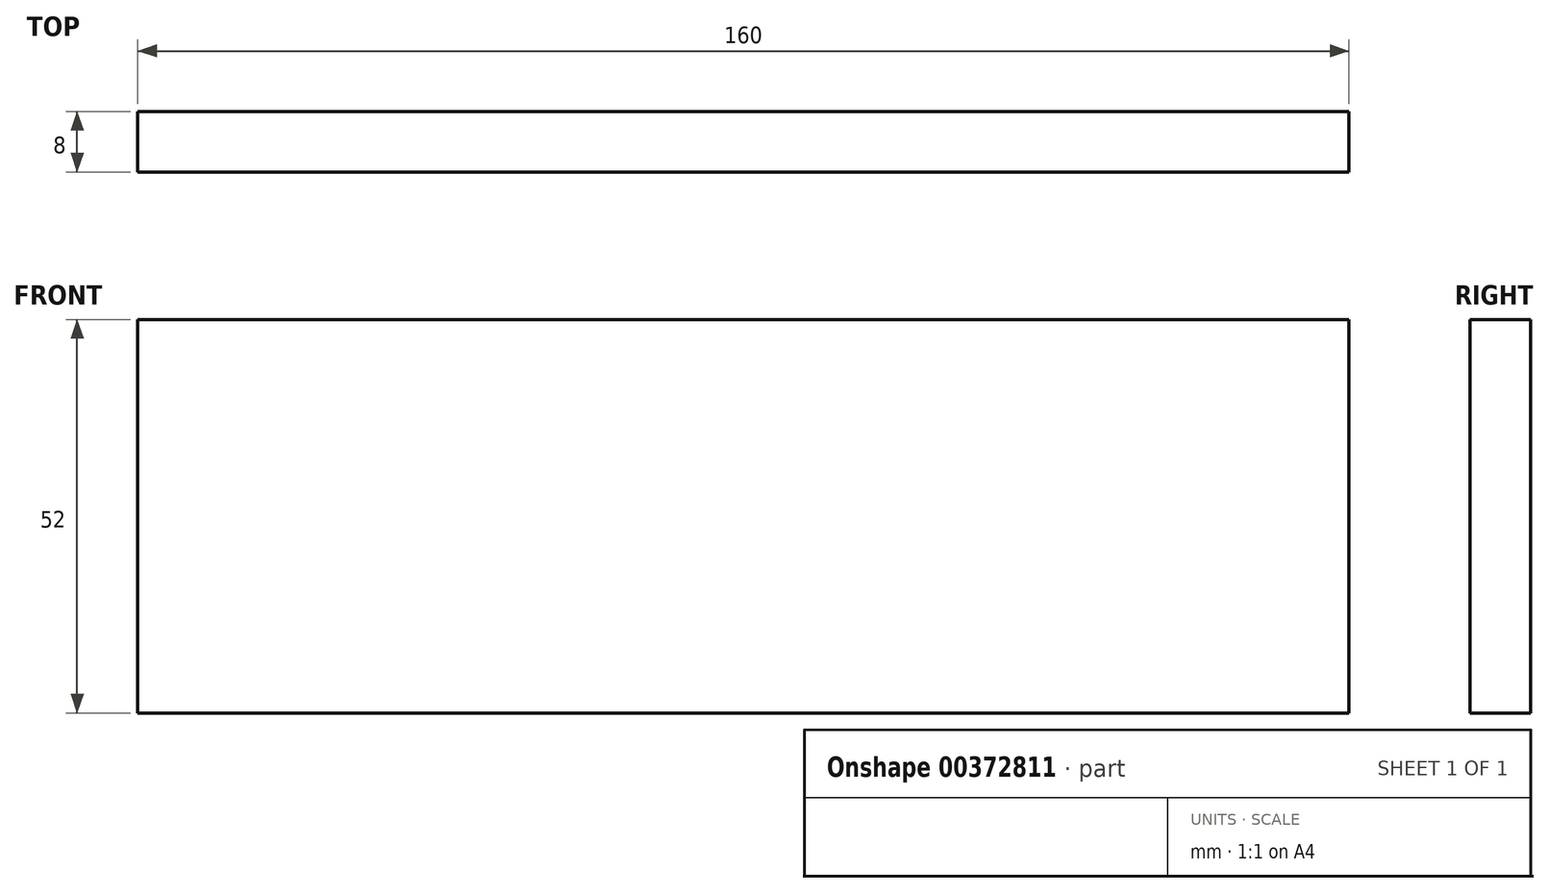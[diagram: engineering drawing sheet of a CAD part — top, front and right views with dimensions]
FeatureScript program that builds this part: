
annotation { "Feature Type Name" : "Feature", "Feature Type Description" : "" }
export const myFeature = defineFeature(function(context is Context, id is Id, definition is map)
    precondition{}
    {
        {
            var Q0;
            Q0=qCreatedBy(makeId("Front.planeOp"),FACE);
            var sketch = newSketch(context, id + "F0", { "sketchPlane" : qUnion([Q0])});
            skLineSegment(sketch, "E0.bottom", {"start": v(80, -26) * mm, "end": v(-80, -26) * mm});
            skLineSegment(sketch, "E0.top", {"start": v(80, 26) * mm, "end": v(-80, 26) * mm});
            skLineSegment(sketch, "E0.left", {"start": v(80, -26) * mm, "end": v(80, 26) * mm});
            skLineSegment(sketch, "E0.right", {"start": v(-80, -26) * mm, "end": v(-80, 26) * mm});
            skPoint(sketch, "E0.middle", {"position": v(0, 0) * mm});
            skSolve(sketch);
        }
        {
            var Q0;
            Q0 = qSketchRegion(id + "F0", true);
            extrude(context, id + "F1", {"entities" : qUnion([Q0]), "endBound" : BoundingType.SYMMETRIC, "depth" : 8 * mm});
        }
    });
